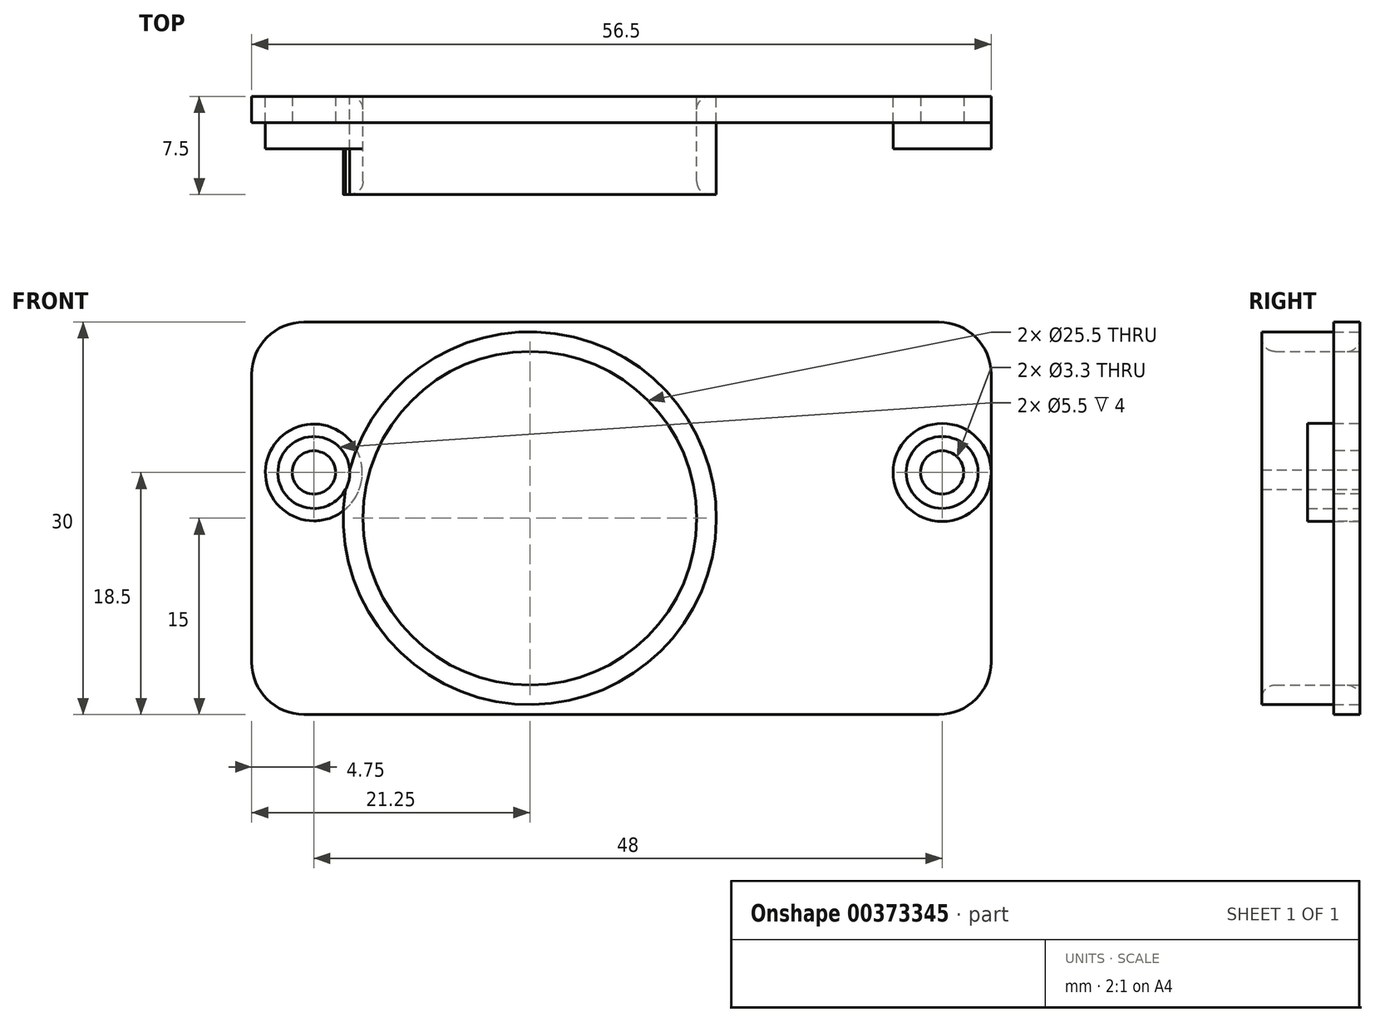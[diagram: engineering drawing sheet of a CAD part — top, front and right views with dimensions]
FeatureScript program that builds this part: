
annotation { "Feature Type Name" : "Feature", "Feature Type Description" : "" }
export const myFeature = defineFeature(function(context is Context, id is Id, definition is map)
    precondition{}
    {
        {
            var Q0;
            Q0=qCreatedBy(makeId("Front.planeOp"),FACE);
            var sketch = newSketch(context, id + "F0", { "sketchPlane" : qUnion([Q0])});
            skLineSegment(sketch, "E0.bottom", {"start": v(24.25, -15) * mm, "end": v(-24.25, -15) * mm});
            skLineSegment(sketch, "E0.top", {"start": v(24.25, 15) * mm, "end": v(-24.25, 15) * mm});
            skLineSegment(sketch, "E0.left", {"start": v(28.25, -11) * mm, "end": v(28.25, 11) * mm});
            skLineSegment(sketch, "E0.right", {"start": v(-28.25, -11) * mm, "end": v(-28.25, 11) * mm});
            skPoint(sketch, "E0.middle", {"position": v(0, 0) * mm});
            skPoint(sketch, "E1.endSnap0", {"position": v(-28.25, 0) * mm});
            skPoint(sketch, "E2", {"position": v(-7, 0) * mm});
            skCircle(sketch, "E3", {"center": v(-7, 0) * mm, "radius": 12.75 * mm});
            skPoint(sketch, "E4", {"position": v(-23.5, 3.5) * mm});
            skPoint(sketch, "E5", {"position": v(24.5, 3.5) * mm});
            skCircle(sketch, "E6", {"center": v(-7, 0) * mm, "radius": 14.25 * mm});
            skCircle(sketch, "E7", {"center": v(-23.5, 3.5) * mm, "radius": 2.75 * mm});
            skCircle(sketch, "E8", {"center": v(-23.5, 3.5) * mm, "radius": 3.7 * mm});
            skCircle(sketch, "E9", {"center": v(24.5, 3.5) * mm, "radius": 2.75 * mm});
            skCircle(sketch, "E10", {"center": v(24.5, 3.5) * mm, "radius": 3.75 * mm});
            skPoint(sketch, "E11.visualSharp", {"position": v(-28.25, 15) * mm});
            skArc(sketch, "E11.filletArc", {"start": v(-24.25, 15) * mm, "mid": v(-27.08, 13.83) * mm, "end": v(-28.25, 11) * mm});
            skPoint(sketch, "E12.visualSharp", {"position": v(28.25, 15) * mm});
            skPoint(sketch, "E13.visualSharp", {"position": v(28.25, -15) * mm});
            skPoint(sketch, "E14.visualSharp", {"position": v(-28.25, -15) * mm});
            skArc(sketch, "E14.filletArc", {"start": v(-28.25, -11) * mm, "mid": v(-27.08, -13.83) * mm, "end": v(-24.25, -15) * mm});
            skArc(sketch, "E15.filletArc", {"start": v(28.25, 11) * mm, "mid": v(27.08, 13.83) * mm, "end": v(24.25, 15) * mm});
            skArc(sketch, "E16.filletArc", {"start": v(24.25, -15) * mm, "mid": v(27.08, -13.83) * mm, "end": v(28.25, -11) * mm});
            skSolve(sketch);
        }
        {
            var Q0;
            Q0=makeQuery(id+"F0.imprint","IMPRINT",FACE,{"disambiguationData":[TD([[makeQuery(id+"F0.imprint","IMPRINT",EDGE,{"derivedFrom":sQuery(id+"F0.wireOp",EDGE,"E7")}),-1.0]])]});
            var Q1;
            Q1=makeQuery(id+"F0.imprint","IMPRINT",FACE,{"disambiguationData":[TD([[makeQuery(id+"F0.imprint","IMPRINT",EDGE,{"derivedFrom":sQuery(id+"F0.wireOp",EDGE,"E9")}),-1.0]])]});
            extrude(context, id + "F1", {"entities" : qUnion([Q0, Q1]), "depth" : 4 * mm});
        }
        {
            var Q0;
            Q0=makeQuery(id+"F0.imprint","IMPRINT",FACE,{"disambiguationData":[TD([[makeQuery(id+"F0.imprint","IMPRINT",EDGE,{"derivedFrom":sQuery(id+"F0.wireOp",EDGE,"E3")}),-1.0]])]});
            var Q1;
            {var subQ0=sQuery(id+"F0.wireOp",EDGE,"E7");var subQ1=sQuery(id+"F0.wireOp",EDGE,"E6");var subQ2=makeQuery(id+"F0.imprint","INTERSECT",VERTEX,{"disambiguationData":[OD(0.0)],"derivedFrom":[subQ1,subQ0]});Q1=makeQuery(id+"F0.imprint","IMPRINT",FACE,{"disambiguationData":[TD([[makeQuery(id+"F0.imprint","IMPRINT",EDGE,{"disambiguationData":[TD([[subQ2,1.0]])],"derivedFrom":subQ1}),1.0]])]});}
            extrude(context, id + "F2", {"entities" : qUnion([Q0, Q1]), "depth" : 7.5 * mm});
        }
        {
            var Q0;
            Q0=makeQuery(id+"F2.opExtrude","CAP_EDGE",EDGE,{"disambiguationData":[OSD([sQuery(id+"F0.wireOp",EDGE,"E3")])],"isStart":false});
            var Q1;
            Q1=makeQuery(id+"F2.opExtrude","CAP_EDGE",EDGE,{"disambiguationData":[OSD([sQuery(id+"F0.wireOp",EDGE,"E3")])],"isStart":true});
            fillet(context, id + "F3", {"entities" : qUnion([Q0, Q1]), "radius" : 1 * mm, "tangentPropagation" : true, "allowEdgeOverflow" : false});
        }
        {
            var Q0;
            Q0=makeQuery(id+"F0.imprint","IMPRINT",FACE,{"disambiguationData":[TD([[makeQuery(id+"F0.imprint","IMPRINT",EDGE,{"derivedFrom":sQuery(id+"F0.wireOp",EDGE,"E0.bottom")}),-1.0]])]});
            var Q1;
            {var subQ0=sQuery(id+"F0.wireOp",EDGE,"E7");var subQ1=sQuery(id+"F0.wireOp",EDGE,"E6");var subQ2=makeQuery(id+"F0.imprint","INTERSECT",VERTEX,{"disambiguationData":[OD(0.0)],"derivedFrom":[subQ1,subQ0]});Q1=makeQuery(id+"F0.imprint","IMPRINT",FACE,{"disambiguationData":[TD([[makeQuery(id+"F0.imprint","IMPRINT",EDGE,{"disambiguationData":[TD([[subQ2,-1.0]])],"derivedFrom":subQ1}),-1.0]])]});}
            var Q2;
            Q2=makeQuery(id+"F0.imprint","IMPRINT",FACE,{"disambiguationData":[TD([[makeQuery(id+"F0.imprint","IMPRINT",EDGE,{"derivedFrom":sQuery(id+"F0.wireOp",EDGE,"E9")}),-1.0]])]});
            var Q3;
            {var subQ0=sQuery(id+"F0.wireOp",EDGE,"E7");var subQ1=sQuery(id+"F0.wireOp",EDGE,"E6");var subQ2=makeQuery(id+"F0.imprint","INTERSECT",VERTEX,{"disambiguationData":[OD(0.0)],"derivedFrom":[subQ1,subQ0]});Q3=makeQuery(id+"F0.imprint","IMPRINT",FACE,{"disambiguationData":[TD([[makeQuery(id+"F0.imprint","IMPRINT",EDGE,{"disambiguationData":[TD([[subQ2,1.0]])],"derivedFrom":subQ1}),-1.0]])]});}
            var Q4;
            {var subQ0=sQuery(id+"F0.wireOp",EDGE,"E7");var subQ1=sQuery(id+"F0.wireOp",EDGE,"E6");var subQ2=makeQuery(id+"F0.imprint","INTERSECT",VERTEX,{"disambiguationData":[OD(0.0)],"derivedFrom":[subQ1,subQ0]});Q4=makeQuery(id+"F0.imprint","IMPRINT",FACE,{"disambiguationData":[TD([[makeQuery(id+"F0.imprint","IMPRINT",EDGE,{"disambiguationData":[TD([[subQ2,1.0]])],"derivedFrom":subQ1}),1.0]])]});}
            var Q5;
            {var subQ0=sQuery(id+"F0.wireOp",EDGE,"E7");var subQ1=sQuery(id+"F0.wireOp",EDGE,"E6");var subQ2=makeQuery(id+"F0.imprint","INTERSECT",VERTEX,{"disambiguationData":[OD(0.0)],"derivedFrom":[subQ1,subQ0]});Q5=makeQuery(id+"F0.imprint","IMPRINT",FACE,{"disambiguationData":[TD([[makeQuery(id+"F0.imprint","IMPRINT",EDGE,{"disambiguationData":[TD([[subQ2,-1.0]])],"derivedFrom":subQ1}),1.0]])]});}
            var Q6;
            Q6=makeQuery(id+"F0.imprint","IMPRINT",FACE,{"disambiguationData":[TD([[makeQuery(id+"F0.imprint","IMPRINT",EDGE,{"derivedFrom":sQuery(id+"F0.wireOp",EDGE,"E3")}),-1.0]])]});
            var Q7;
            Q7=makeQuery(id+"F0.imprint","IMPRINT",FACE,{"disambiguationData":[TD([[makeQuery(id+"F0.imprint","IMPRINT",EDGE,{"derivedFrom":sQuery(id+"F0.wireOp",EDGE,"E9")}),1.0]])]});
            extrude(context, id + "F4", {"entities" : qUnion([Q0, Q1, Q2, Q3, Q4, Q5, Q6, Q7]), "depth" : 2 * mm});
        }
        {
            var Q0;
            Q0=sQuery(id+"F0.wireOp",VERTEX,"E5");
            var Q1;
            Q1=sQuery(id+"F0.wireOp",VERTEX,"E4");
            var Q2;
            Q2=makeQuery(id+"F4.opExtrude","SWEPT_BODY",BODY,{"disambiguationData":[OSD([sQuery(id+"F0.wireOp",EDGE,"E0.bottom"),sQuery(id+"F0.wireOp",EDGE,"E0.top"),sQuery(id+"F0.wireOp",EDGE,"E0.left"),sQuery(id+"F0.wireOp",EDGE,"E0.right"),sQuery(id+"F0.wireOp",EDGE,"E3"),sQuery(id+"F0.wireOp",EDGE,"E11.filletArc"),sQuery(id+"F0.wireOp",EDGE,"E14.filletArc"),sQuery(id+"F0.wireOp",EDGE,"E15.filletArc"),sQuery(id+"F0.wireOp",EDGE,"E16.filletArc")])]});
            hole(context, id + "F5", {"style" : HoleStyle.SIMPLE, "endStyle" : HoleEndStyle.BLIND, "oppositeDirection" : true, "standardTappedOrClearance" : lookupTablePath({ "standard" : "ISO", "fit" : "Normal", "size" : "M3", "type" : "Clearance" }), "standardBlindInLast" : lookupTablePath({ "fit" : "Standard", "standard" : "ISO", "size" : "M3", "type" : "Clearance" }), "holeDiameter" : 3.3 * mm, "holeDepth" : 13.5 * mm, "tappedDepth" : 12 * mm, "tapClearance" : 3, "locations" : qUnion([Q0, Q1]), "scope" : qUnion([Q2])});
        }
    });
